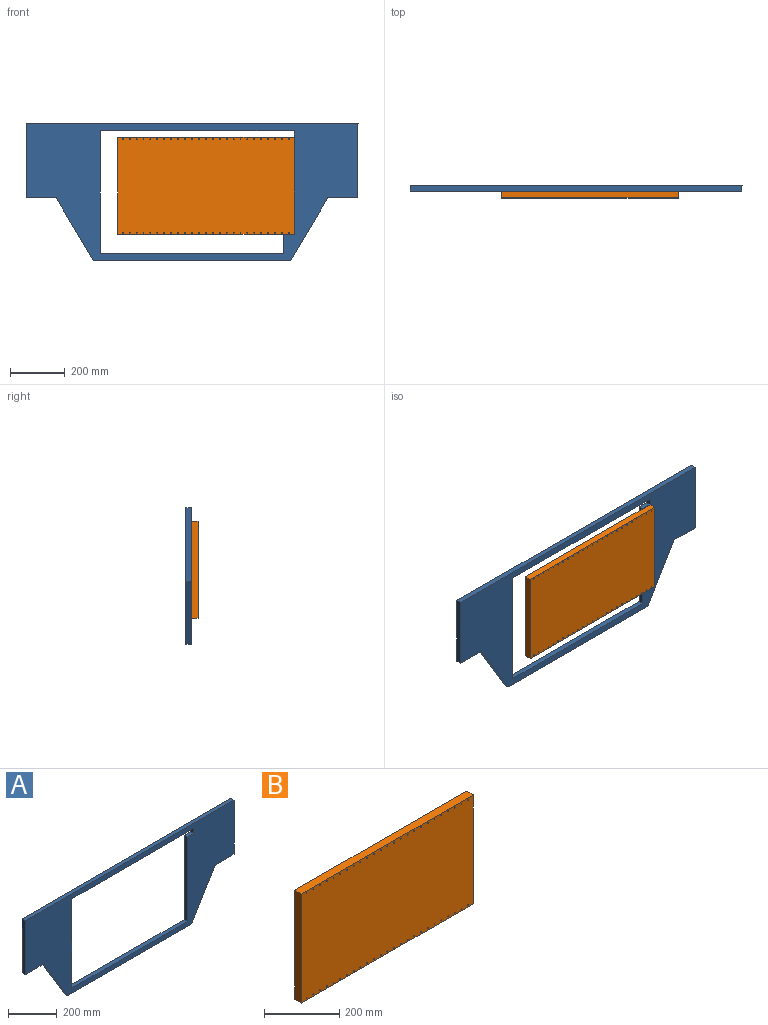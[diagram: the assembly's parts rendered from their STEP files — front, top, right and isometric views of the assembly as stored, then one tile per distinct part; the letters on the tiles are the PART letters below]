
ASSEMBLY  parts=2 mates=1
PART A: 16 faces, bbox 1217.1x19.1x501.7 mm
  f0: plane 25.4x19.05mm, normal (-1,0,0), area 483.9mm2, adj f1,f13,f14,f15
  f1: plane 38.1x19.05mm, normal (0,0,1), area 725.8mm2, adj f0,f2,f14,f15
  f2: plane 425.45x19.05mm, normal (-1,0,0), area 8104.8mm2, adj f1,f3,f14,f15
  f3: plane 673.1x19.05mm, normal (0,0,1), area 12822.6mm2, adj f2,f4,f14,f15
  f4: plane 450.85x19.05mm, normal (1,0,0), area 8588.7mm2, adj f3,f13,f14,f15
  f5: plane 229.17x136.04mm, normal (-0.86,0,-0.51), area 5077mm2, adj f6,f12,f14,f15
  f6: plane 723.9x19.05mm, normal (0,0,-1), area 13790.3mm2, adj f5,f7,f14,f15
  f7: plane 229.17x136.04mm, normal (0.86,0,-0.51), area 5077mm2, adj f6,f8,f14,f15
  f8: plane 110.58x19.05mm, normal (0,0,-1), area 2106.5mm2, adj f7,f9,f14,f15
  f9: plane 272.48x19.05mm, normal (1,0,0), area 5190.7mm2, adj f8,f10,f14,f15
  f10: plane 1217.14x19.05mm, normal (0,0,1), area 23186.5mm2, adj f9,f11,f14,f15
  f11: plane 272.48x19.05mm, normal (-1,0,0), area 5190.7mm2, adj f10,f12,f14,f15
  f12: plane 110.58x19.05mm, normal (0,0,-1), area 2106.5mm2, adj f5,f11,f14,f15
  f13: plane 711.2x19.05mm, normal (0,0,-1), area 13548.4mm2, adj f0,f4,f14,f15
  f14: plane 1217.14x501.65mm, normal (0,-1,0), area 224284.1mm2, adj f0,f1,f2,f3,f4,f5,f6,f7
  f15: plane 1217.14x501.65mm, normal (0,1,0), area 224284.1mm2, adj f0,f1,f2,f3,f4,f5,f6,f7
PART B: 56 faces, bbox 647.7x25.4x355.6 mm
  f0: plane 647.7x25.4mm, normal (0,0,1), area 16451.6mm2, adj f1,f53,f54,f55
  f1: plane 355.6x25.4mm, normal (-1,0,0), area 9032.2mm2, adj f0,f2,f54,f55
  f2: plane 647.7x25.4mm, normal (0,0,-1), area 16451.6mm2, adj f1,f53,f54,f55
  f3: cylinder r=1.59mm len=25.4mm, axis (0,1,0), area 253.4mm2, adj f54,f55
  f4: cylinder r=1.59mm len=25.4mm, axis (0,1,0), area 253.4mm2, adj f54,f55
  f5: cylinder r=1.59mm len=25.4mm, axis (0,1,0), area 253.4mm2, adj f54,f55
  f6: cylinder r=1.59mm len=25.4mm, axis (0,1,0), area 253.4mm2, adj f54,f55
  f7: cylinder r=1.59mm len=25.4mm, axis (0,1,0), area 253.4mm2, adj f54,f55
  f8: cylinder r=1.59mm len=25.4mm, axis (0,1,0), area 253.4mm2, adj f54,f55
  f9: cylinder r=1.59mm len=25.4mm, axis (0,1,0), area 253.4mm2, adj f54,f55
  f10: cylinder r=1.59mm len=25.4mm, axis (0,1,0), area 253.4mm2, adj f54,f55
  f11: cylinder r=1.59mm len=25.4mm, axis (0,1,0), area 253.4mm2, adj f54,f55
  f12: cylinder r=1.59mm len=25.4mm, axis (0,1,0), area 253.4mm2, adj f54,f55
  f13: cylinder r=1.59mm len=25.4mm, axis (0,1,0), area 253.4mm2, adj f54,f55
  f14: cylinder r=1.59mm len=25.4mm, axis (0,1,0), area 253.4mm2, adj f54,f55
  f15: cylinder r=1.59mm len=25.4mm, axis (0,1,0), area 253.4mm2, adj f54,f55
  f16: cylinder r=1.59mm len=25.4mm, axis (0,1,0), area 253.4mm2, adj f54,f55
  f17: cylinder r=1.59mm len=25.4mm, axis (0,1,0), area 253.4mm2, adj f54,f55
  f18: cylinder r=1.59mm len=25.4mm, axis (0,1,0), area 253.4mm2, adj f54,f55
  f19: cylinder r=1.59mm len=25.4mm, axis (0,1,0), area 253.4mm2, adj f54,f55
  f20: cylinder r=1.59mm len=25.4mm, axis (0,1,0), area 253.4mm2, adj f54,f55
  f21: cylinder r=1.59mm len=25.4mm, axis (0,1,0), area 253.4mm2, adj f54,f55
  f22: cylinder r=1.59mm len=25.4mm, axis (0,1,0), area 253.4mm2, adj f54,f55
  f23: cylinder r=1.59mm len=25.4mm, axis (0,1,0), area 253.4mm2, adj f54,f55
  f24: cylinder r=1.59mm len=25.4mm, axis (0,1,0), area 253.4mm2, adj f54,f55
  f25: cylinder r=1.59mm len=25.4mm, axis (0,1,0), area 253.4mm2, adj f54,f55
  f26: cylinder r=1.59mm len=25.4mm, axis (0,1,0), area 253.4mm2, adj f54,f55
  f27: cylinder r=1.59mm len=25.4mm, axis (0,1,0), area 253.4mm2, adj f54,f55
  f28: cylinder r=1.59mm len=25.4mm, axis (0,1,0), area 253.4mm2, adj f54,f55
  f29: cylinder r=1.59mm len=25.4mm, axis (0,1,0), area 253.4mm2, adj f54,f55
  f30: cylinder r=1.59mm len=25.4mm, axis (0,1,0), area 253.4mm2, adj f54,f55
  f31: cylinder r=1.59mm len=25.4mm, axis (0,1,0), area 253.4mm2, adj f54,f55
  f32: cylinder r=1.59mm len=25.4mm, axis (0,1,0), area 253.4mm2, adj f54,f55
  f33: cylinder r=1.59mm len=25.4mm, axis (0,1,0), area 253.4mm2, adj f54,f55
  f34: cylinder r=1.59mm len=25.4mm, axis (0,1,0), area 253.4mm2, adj f54,f55
  f35: cylinder r=1.59mm len=25.4mm, axis (0,1,0), area 253.4mm2, adj f54,f55
  f36: cylinder r=1.59mm len=25.4mm, axis (0,1,0), area 253.4mm2, adj f54,f55
  f37: cylinder r=1.59mm len=25.4mm, axis (0,1,0), area 253.4mm2, adj f54,f55
  f38: cylinder r=1.59mm len=25.4mm, axis (0,1,0), area 253.4mm2, adj f54,f55
  f39: cylinder r=1.59mm len=25.4mm, axis (0,1,0), area 253.4mm2, adj f54,f55
  f40: cylinder r=1.59mm len=25.4mm, axis (0,1,0), area 253.4mm2, adj f54,f55
  f41: cylinder r=1.59mm len=25.4mm, axis (0,1,0), area 253.4mm2, adj f54,f55
  f42: cylinder r=1.59mm len=25.4mm, axis (0,1,0), area 253.4mm2, adj f54,f55
  f43: cylinder r=1.59mm len=25.4mm, axis (0,1,0), area 253.4mm2, adj f54,f55
  f44: cylinder r=1.59mm len=25.4mm, axis (0,1,0), area 253.4mm2, adj f54,f55
  f45: cylinder r=1.59mm len=25.4mm, axis (0,1,0), area 253.4mm2, adj f54,f55
  f46: cylinder r=1.59mm len=25.4mm, axis (0,1,0), area 253.4mm2, adj f54,f55
  f47: cylinder r=1.59mm len=25.4mm, axis (0,1,0), area 253.4mm2, adj f54,f55
  f48: cylinder r=1.59mm len=25.4mm, axis (0,1,0), area 253.4mm2, adj f54,f55
  f49: cylinder r=1.59mm len=25.4mm, axis (0,1,0), area 253.4mm2, adj f54,f55
  f50: cylinder r=1.59mm len=25.4mm, axis (0,1,0), area 253.4mm2, adj f54,f55
  f51: cylinder r=1.59mm len=25.4mm, axis (0,1,0), area 253.4mm2, adj f54,f55
  f52: cylinder r=1.59mm len=25.4mm, axis (0,1,0), area 253.4mm2, adj f54,f55
  f53: plane 355.6x25.4mm, normal (1,0,0), area 9032.2mm2, adj f0,f2,f54,f55
  f54: plane 647.7x355.6mm, normal (0,-1,0), area 229926.3mm2, adj f0,f1,f2,f3,f4,f5,f6,f7
  f55: plane 647.7x355.6mm, normal (0,1,0), area 229926.3mm2, adj f0,f1,f2,f3,f4,f5,f6,f7
PLACE A t=(176.19,28.57,199.56)mm
PLACE B t=(113.49,9.52,320.7)mm
MATE fastened B.f0 <-> A.f1  axis (0,0,1) through (246.71,9.52,570.07)mm
